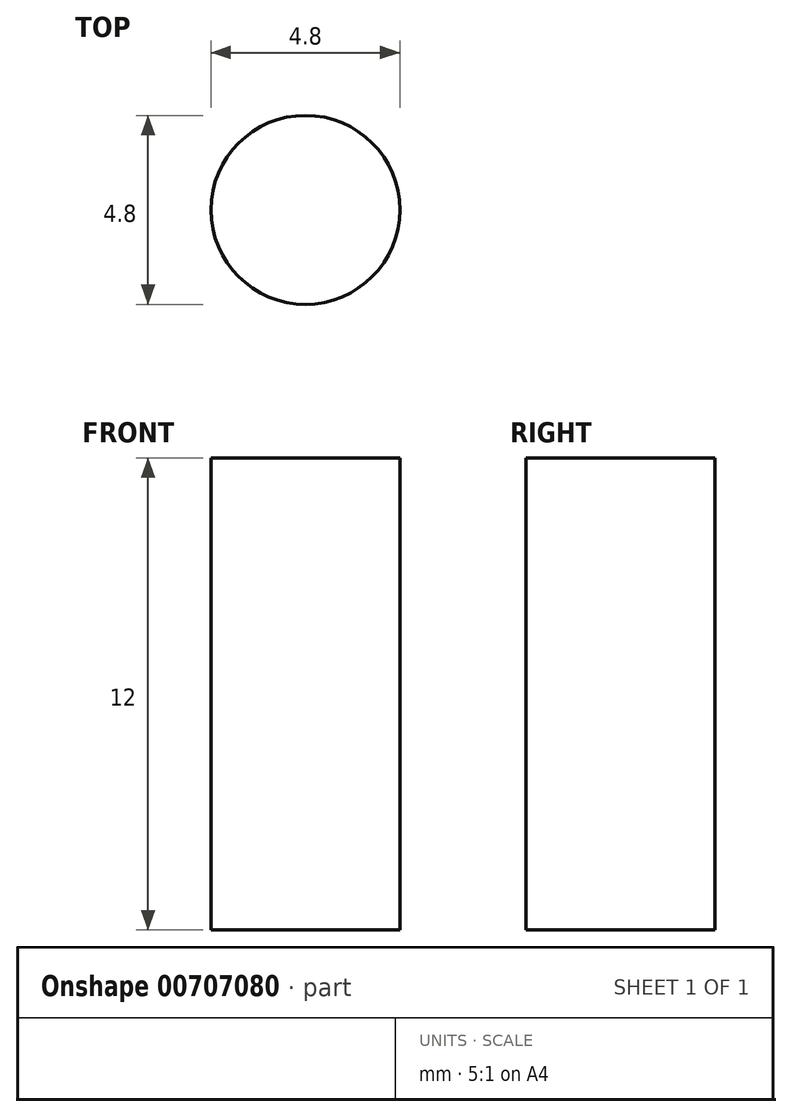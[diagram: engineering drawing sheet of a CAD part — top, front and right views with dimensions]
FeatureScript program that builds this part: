
annotation { "Feature Type Name" : "Feature", "Feature Type Description" : "" }
export const myFeature = defineFeature(function(context is Context, id is Id, definition is map)
    precondition{}
    {
        {
            var Q0;
            Q0=qCreatedBy(makeId("Top.planeOp"),FACE);
            var sketch = newSketch(context, id + "F0", { "sketchPlane" : qUnion([Q0])});
            skCircle(sketch, "E0", {"center": v(0, 0) * mm, "radius": 2.4 * mm});
            skSolve(sketch);
        }
        {
            var Q0;
            Q0 = qSketchRegion(id + "F0", true);
            extrude(context, id + "F1", {"entities" : qUnion([Q0]), "depth" : 12 * mm, "offsetDistance" : 25.4 * mm});
        }
    });
